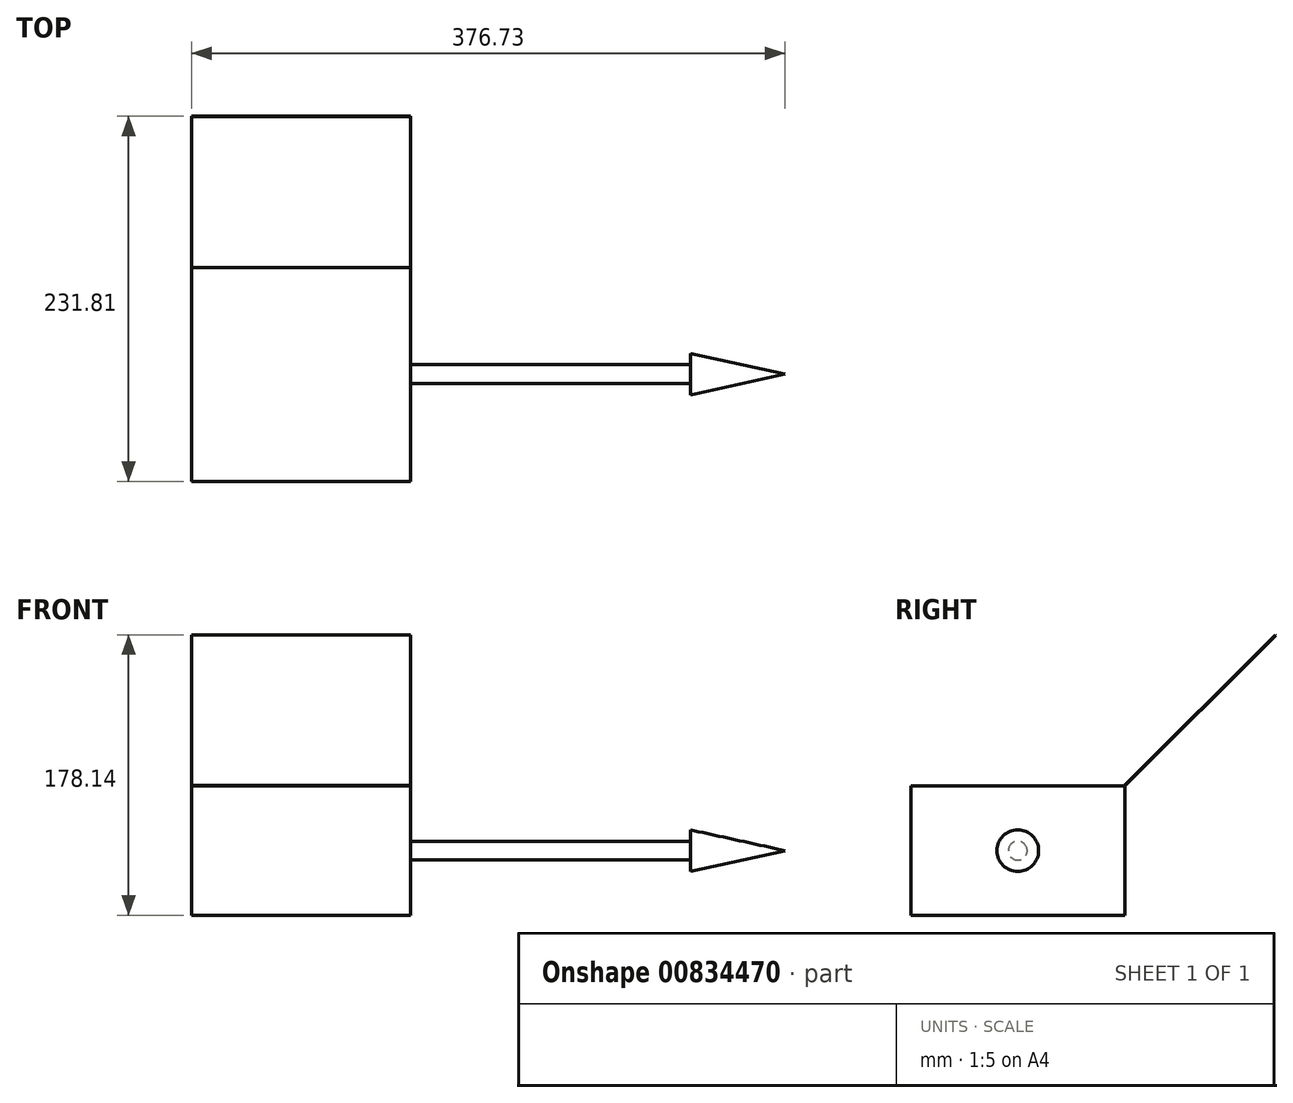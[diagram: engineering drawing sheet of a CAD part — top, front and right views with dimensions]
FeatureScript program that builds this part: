
annotation { "Feature Type Name" : "Feature", "Feature Type Description" : "" }
export const myFeature = defineFeature(function(context is Context, id is Id, definition is map)
    precondition{}
    {
        {
            var Q0;
            Q0=qCreatedBy(makeId("Top.planeOp"),FACE);
            var sketch = newSketch(context, id + "F0", { "sketchPlane" : qUnion([Q0])});
            skLineSegment(sketch, "E0.bottom", {"start": v(0, -0.87) * mm, "end": v(139, -0.87) * mm});
            skLineSegment(sketch, "E0.top", {"start": v(0, -136.87) * mm, "end": v(139, -136.87) * mm});
            skLineSegment(sketch, "E0.left", {"start": v(0, -0.87) * mm, "end": v(0, -136.87) * mm});
            skLineSegment(sketch, "E0.right", {"start": v(139, -0.87) * mm, "end": v(139, -136.87) * mm});
            skSolve(sketch);
        }
        {
            var Q0;
            Q0=makeQuery(id+"F0.imprint","IMPRINT",FACE,{"disambiguationData":[TD([[makeQuery(id+"F0.imprint","IMPRINT",EDGE,{"derivedFrom":sQuery(id+"F0.wireOp",EDGE,"E0.bottom")}),-1.0]])]});
            extrude(context, id + "F1", {"entities" : qUnion([Q0]), "depth" : 82 * mm, "offsetDistance" : 25.4 * mm});
        }
        {
            var Q0;
            Q0=makeQuery(id+"F1.opExtrude","CAP_EDGE",EDGE,{"disambiguationData":[OSD([sQuery(id+"F0.wireOp",EDGE,"E0.bottom")])],"isStart":false});
            cPlane(context, id + "F2", {"entities" : qUnion([Q0]), "cplaneType" : CPlaneType.LINE_ANGLE, "offset" : 25.4 * mm, "angle" : 135 * degree, "width" : 152.4 * mm, "height" : 152.4 * mm});
        }
        {
            var Q0;
            Q0=qCreatedBy(id+"F2.planeOp",FACE);
            var sketch = newSketch(context, id + "F3", { "sketchPlane" : qUnion([Q0])});
            skLineSegment(sketch, "E1.bottom", {"start": v(0, 57.37) * mm, "end": v(139, 57.37) * mm});
            skLineSegment(sketch, "E1.top", {"start": v(0, 192.87) * mm, "end": v(139, 192.87) * mm});
            skLineSegment(sketch, "E1.left", {"start": v(0, 57.37) * mm, "end": v(0, 192.87) * mm});
            skLineSegment(sketch, "E1.right", {"start": v(139, 57.37) * mm, "end": v(139, 192.87) * mm});
            skSolve(sketch);
        }
        {
            var Q0;
            Q0=makeQuery(id+"F3.imprint","IMPRINT",FACE,{"disambiguationData":[TD([[makeQuery(id+"F3.imprint","IMPRINT",EDGE,{"derivedFrom":sQuery(id+"F3.wireOp",EDGE,"E1.bottom")}),1.0]])]});
            extrude(context, id + "F4", {"entities" : qUnion([Q0]), "depth" : 0.46 * mm, "offsetDistance" : 25.4 * mm});
        }
        {
            var Q0;
            Q0=makeQuery(id+"F1.opExtrude","SWEPT_FACE",FACE,{"disambiguationData":[OSD([sQuery(id+"F0.wireOp",EDGE,"E0.right")])]});
            var sketch = newSketch(context, id + "F5", { "sketchPlane" : qUnion([Q0])});
            skLineSegment(sketch, "E2", {"start": v(-136.87, 41) * mm, "end": v(-0.87, 41) * mm, "construction": true});
            skLineSegment(sketch, "E3", {"start": v(-68.87, 82) * mm, "end": v(-68.87, 0) * mm, "construction": true});
            skCircle(sketch, "E4", {"center": v(-68.87, 41) * mm, "radius": 6 * mm});
            skSolve(sketch);
        }
        {
            var Q0;
            Q0 = qSketchRegion(id + "F5", true);
            extrude(context, id + "F6", {"entities" : qUnion([Q0]), "depth" : 177.8 * mm, "offsetDistance" : 25.4 * mm});
        }
        {
            var Q0;
            Q0=makeQuery(id+"F6.opExtrude","SWEPT_FACE",FACE,{"disambiguationData":[OSD([sQuery(id+"F5.wireOp",EDGE,"E4")])]});
            cPlane(context, id + "F7", {"entities" : qUnion([Q0]), "cplaneType" : CPlaneType.LINE_ANGLE, "offset" : 25.4 * mm, "angle" : 0 * degree, "width" : 152.4 * mm, "height" : 152.4 * mm});
        }
        {
            var Q0;
            Q0=qCreatedBy(id+"F7.planeOp",FACE);
            var sketch = newSketch(context, id + "F8", { "sketchPlane" : qUnion([Q0])});
            skLineSegment(sketch, "E5", {"start": v(316.8, 41) * mm, "end": v(376.73, 41) * mm});
            skLineSegment(sketch, "E6", {"start": v(376.73, 41) * mm, "end": v(316.8, 27.79) * mm});
            skLineSegment(sketch, "E7", {"start": v(316.8, 27.79) * mm, "end": v(316.8, 41) * mm});
            skLineSegment(sketch, "E8", {"start": v(139, 41) * mm, "end": v(316.8, 41) * mm, "construction": true});
            skSolve(sketch);
        }
        {
            var Q0;
            Q0=makeQuery(id+"F8.imprint","IMPRINT",FACE,{"disambiguationData":[TD([[makeQuery(id+"F8.imprint","IMPRINT",EDGE,{"derivedFrom":sQuery(id+"F8.wireOp",EDGE,"E5")}),-1.0]])]});
            var Q1;
            Q1=sQuery(id+"F8.wireOp",EDGE,"E8");
            revolve(context, id + "F9", {"operationType" : NewBodyOperationType.ADD, "surfaceOperationType" : NewSurfaceOperationType.NEW, "entities" : qUnion([Q0]), "axis" : qUnion([Q1]), "revolveType" : RevolveType.FULL});
        }
    });
